# Revit family: EBRE-LED 414x-MPSx
name_source: partatom
category: Leuchten
units: mm (PartAtom-declared; Revit-internal decimal feet)

## family parameters
Basisbauteil = Fläche
Beim Laden mit Abzugskörper schneiden = Nein
Bemaßung runder Anschluss = Durchmesser verwenden
Gemeinsam genutzt = Nein
Lichtquelle = Ja
OmniClass-Nummer = 23.80.70.11
OmniClass-Titel = Luminaries for Internal Lighting
Raumberechnungspunkt = Nein
Teiletyp = Normal

## types (8) — shared parameters
Baugruppenkennzeichen = D5020200
Datei für fotometrisches Netz = EBRE-LED 2285200-840 MPS.IES
Emissionsform beim Rendern sichtbar = Nein
Farbfilter = 16777215
Farbtemperaturverschiebung bei Dämpfen der Lampe = <Keine Auswahl>
Hersteller = RIDI Leuchten GmbH
Lampe = LED
Neigungswinkel = 90.00°
URL = www.ridi.de
Von Breite des Rechtecks ausssenden = 560 mm  [stored 1.83727 ft]
Von Länge des Rechtecks aussenden = 560 mm  [stored 1.83727 ft]
brand = RIDI
conformity mark = CE
electrical safety class = 1
height = 60 mm  [stored 0.19685 ft]
ingress protection (IP) code = IP20
length = 622 mm  [stored 2.04068 ft]
nominal frequency = 50-60Hz
nominal voltage = 230
voltage type (AC, DC, UC) = AC
weight = 6,4kg
width = 622 mm  [stored 2.04068 ft]
zero-valued in all types: Vorgabe-Ansicht

## per-type parameters (varying)
| type | Modell | Scheinlast | product name | rated input power |
| EBRE-LED 414/2500-830 MPS | 0822888 | 16 VA | EBRE-LED 414/6200-840 MPO-DA | 16 |
| EBRE-LED 414/2500-830 MPS-DA | 0832888 | 16 VA | EBRE-LED 414/2500-830 MPS-DA | 16 |
| EBRE-LED 414/2700-840 MPS | 0822889 | 16 VA | EBRE-LED 414/2700-840 MPS | 16 |
| EBRE-LED 414/2700-840 MPS-DA | 0832889 | 16 VA | EBRE-LED 414/2700-840 MPS-DA | 16 |
| EBRE-LED 414/5000-830 MPS | 0822890 | 32 VA | EBRE-LED 414/5000-830 MPS | 32 |
| EBRE-LED 414/5000-830 MPS-DA | 0832890 | 32 VA | EBRE-LED 414/5000-830 MPS-DA | 32 |
| EBRE-LED 414/5200-840 MPS | 0822832 | 32 VA | EBRE-LED 414/5200-840 MPS | 32 |
| EBRE-LED 414/5200-840 MPS-DA | 0832832 | 32 VA | EBRE-LED 414/5200-840 MPS-DA | 32 |

note: [stored X ft] marks values corroborated as IEEE doubles in the binary element streams (Revit-internal decimal feet)
